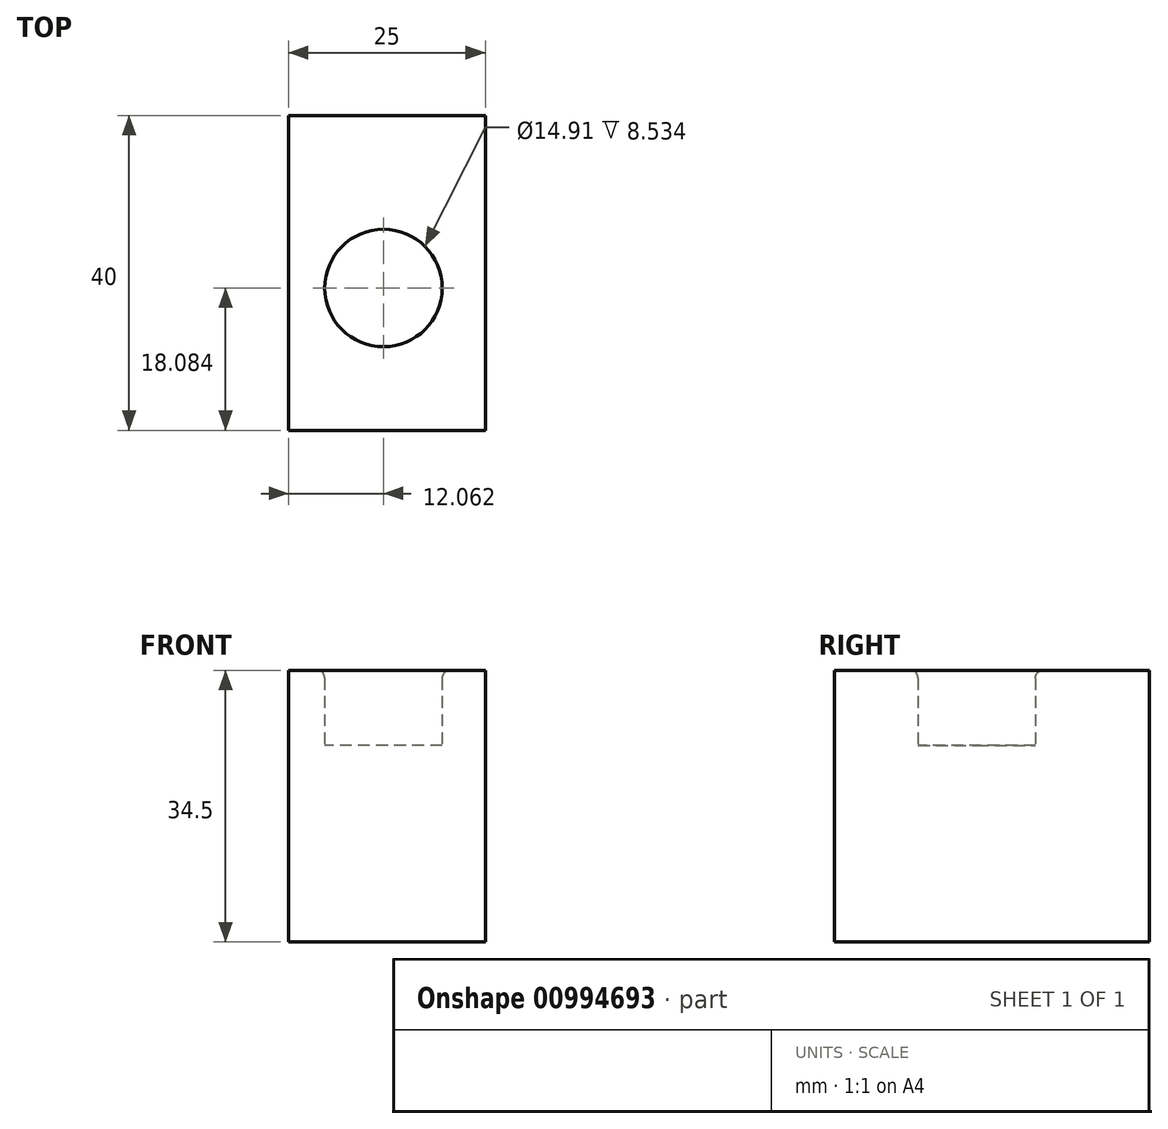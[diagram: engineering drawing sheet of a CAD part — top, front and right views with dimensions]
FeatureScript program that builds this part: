
annotation { "Feature Type Name" : "Feature", "Feature Type Description" : "" }
export const myFeature = defineFeature(function(context is Context, id is Id, definition is map)
    precondition{}
    {
        {
            var Q0;
            Q0=qCreatedBy(makeId("Top.planeOp"),FACE);
            var sketch = newSketch(context, id + "F0", { "sketchPlane" : qUnion([Q0])});
            skLineSegment(sketch, "E0.bottom", {"start": v(-11.9, 21.83) * mm, "end": v(13.1, 21.83) * mm});
            skLineSegment(sketch, "E0.top", {"start": v(-11.9, -18.17) * mm, "end": v(13.1, -18.17) * mm});
            skLineSegment(sketch, "E0.left", {"start": v(-11.9, 21.83) * mm, "end": v(-11.9, -18.17) * mm});
            skLineSegment(sketch, "E0.right", {"start": v(13.1, 21.83) * mm, "end": v(13.1, -18.17) * mm});
            skLineSegment(sketch, "E1", {"start": v(0, 29.82) * mm, "end": v(0, 5.63) * mm, "construction": true});
            skSolve(sketch);
        }
        {
            var Q0;
            Q0=makeQuery(id+"F0.imprint","IMPRINT",FACE,{"disambiguationData":[TD([[makeQuery(id+"F0.imprint","IMPRINT",EDGE,{"derivedFrom":sQuery(id+"F0.wireOp",EDGE,"E0.bottom")}),-1.0]])]});
            extrude(context, id + "F1", {"entities" : qUnion([Q0]), "depth" : 25 * mm, "offsetDistance" : 25 * mm});
        }
        {
            var Q0;
            Q0=makeQuery(id+"F1.opExtrude","CAP_FACE",FACE,{"disambiguationData":[OSD([sQuery(id+"F0.wireOp",EDGE,"E0.bottom"),sQuery(id+"F0.wireOp",EDGE,"E0.top"),sQuery(id+"F0.wireOp",EDGE,"E0.left"),sQuery(id+"F0.wireOp",EDGE,"E0.right")])],"isStart":false});
            var sketch = newSketch(context, id + "F2", { "sketchPlane" : qUnion([Q0])});
            skCircle(sketch, "E2", {"center": v(0.15, -0.09) * mm, "radius": 7.46 * mm});
            skPoint(sketch, "E2.first.point", {"position": v(7.6, 0) * mm});
            skPoint(sketch, "E2.second.point", {"position": v(-7.3, 0) * mm});
            skPoint(sketch, "E2.third.point", {"position": v(0, 7.37) * mm});
            skSolve(sketch);
        }
        {
            var Q0;
            Q0=makeQuery(id+"F2.imprint","IMPRINT",FACE,{"disambiguationData":[TD([[makeQuery(id+"F2.imprint","IMPRINT",EDGE,{"derivedFrom":sQuery(id+"F2.wireOp",EDGE,"E2")}),-1.0]])]});
            extrude(context, id + "F3", {"entities" : qUnion([Q0]), "operationType" : NewBodyOperationType.ADD, "depth" : 9.5 * mm, "offsetDistance" : 25 * mm});
        }
        {
            var Q0;
            Q0=makeQuery(id+"F2.imprint","IMPRINT",FACE,{"disambiguationData":[TD([[makeQuery(id+"F2.imprint","IMPRINT",EDGE,{"derivedFrom":sQuery(id+"F2.wireOp",EDGE,"E2")}),1.0]])]});
            var sketch = newSketch(context, id + "F4", { "sketchPlane" : qUnion([Q0])});
            skSolve(sketch);
        }
        {
            var Q0;
            Q0=makeQuery(id+"F3.opExtrude","CAP_EDGE",EDGE,{"disambiguationData":[OSD([sQuery(id+"F2.wireOp",EDGE,"E2")])],"isStart":false});
            fillet(context, id + "F5", {"entities" : qUnion([Q0]), "radius" : 0.97 * mm, "tangentPropagation" : true, "allowEdgeOverflow" : false});
        }
        {
            var Q0;
            Q0=makeQuery(id+"F3.opExtrude","CAP_FACE",FACE,{"disambiguationData":[OSD([sQuery(id+"F0.wireOp",EDGE,"E0.bottom"),sQuery(id+"F0.wireOp",EDGE,"E0.top"),sQuery(id+"F0.wireOp",EDGE,"E0.left"),sQuery(id+"F0.wireOp",EDGE,"E0.right"),sQuery(id+"F2.wireOp",EDGE,"E2")])],"isStart":false});
            var sketch = newSketch(context, id + "F6", { "sketchPlane" : qUnion([Q0])});
            skCircle(sketch, "E3", {"center": v(-6.28, 15.47) * mm, "radius": 3.56 * mm});
            skCircle(sketch, "E4", {"center": v(7.73, 15.05) * mm, "radius": 3.81 * mm});
            skSolve(sketch);
        }
        {
            var Q0;
            Q0=sQuery(id+"F6.wireOp",EDGE,"E3");
            var Q1;
            Q1=sQuery(id+"F6.wireOp",EDGE,"E4");
            extrude(context, id + "F7", {"bodyType" : ToolBodyType.SURFACE, "surfaceEntities" : qUnion([Q0, Q1]), "oppositeDirection" : true, "depth" : 2.9 * mm, "offsetDistance" : 25 * mm});
        }
    });
